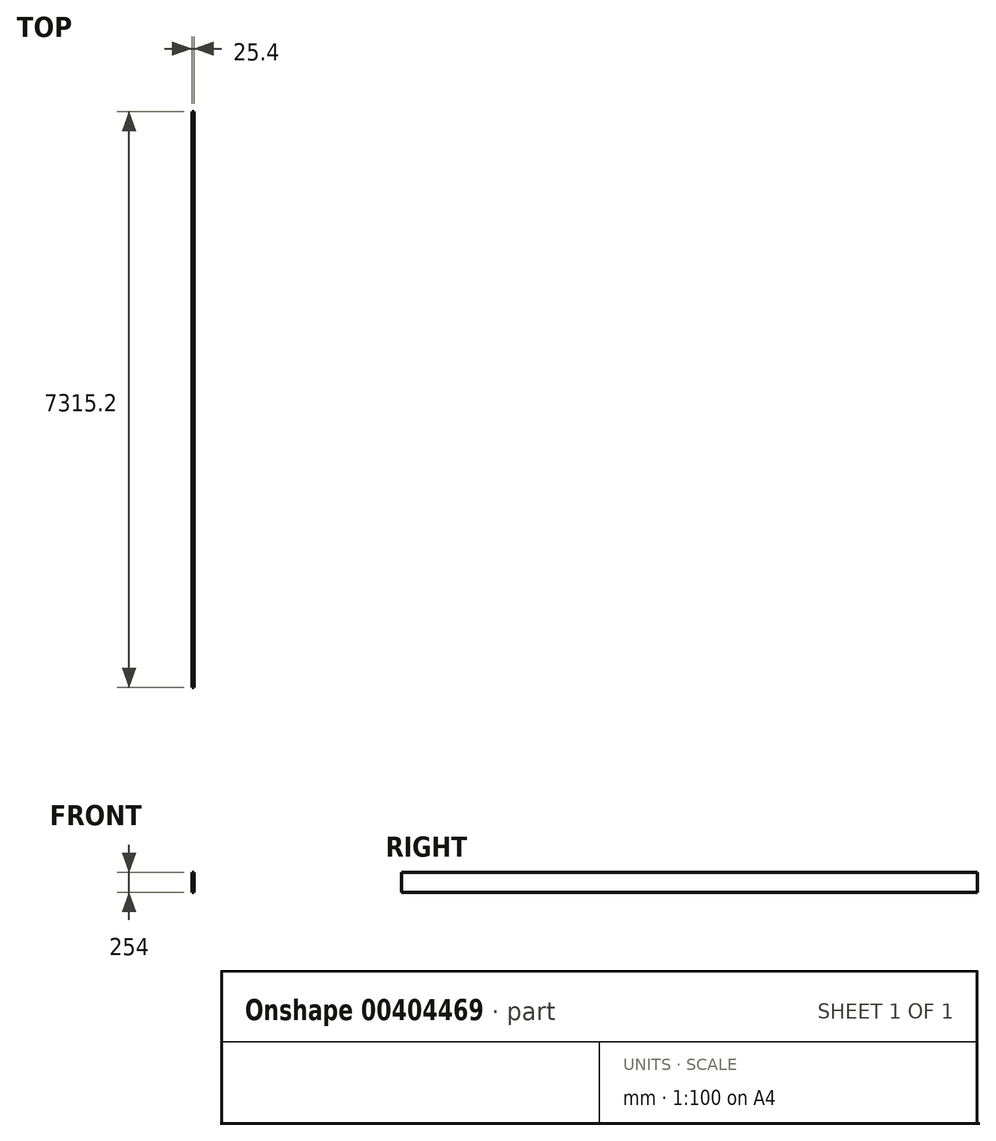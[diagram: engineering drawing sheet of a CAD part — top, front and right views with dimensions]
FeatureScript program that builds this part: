
annotation { "Feature Type Name" : "Feature", "Feature Type Description" : "" }
export const myFeature = defineFeature(function(context is Context, id is Id, definition is map)
    precondition{}
    {
        {
            var Q0;
            Q0=qCreatedBy(makeId("Front.planeOp"),FACE);
            var sketch = newSketch(context, id + "F0", { "sketchPlane" : qUnion([Q0])});
            skLineSegment(sketch, "E0", {"start": v(0, 0) * mm, "end": v(25.4, 0) * mm});
            skLineSegment(sketch, "E1", {"start": v(25.4, 0) * mm, "end": v(25.4, -254) * mm});
            skLineSegment(sketch, "E2", {"start": v(25.4, -254) * mm, "end": v(0, -254) * mm});
            skLineSegment(sketch, "E3", {"start": v(0, -254) * mm, "end": v(0, 0) * mm});
            skSolve(sketch);
        }
        {
            var Q0;
            Q0=makeQuery(id+"F0.imprint","IMPRINT",FACE,{"disambiguationData":[TD([[makeQuery(id+"F0.imprint","IMPRINT",EDGE,{"derivedFrom":sQuery(id+"F0.wireOp",EDGE,"E0")}),-1.0]])]});
            extrude(context, id + "F1", {"entities" : qUnion([Q0]), "depth" : 7315.2 * mm});
        }
    });
